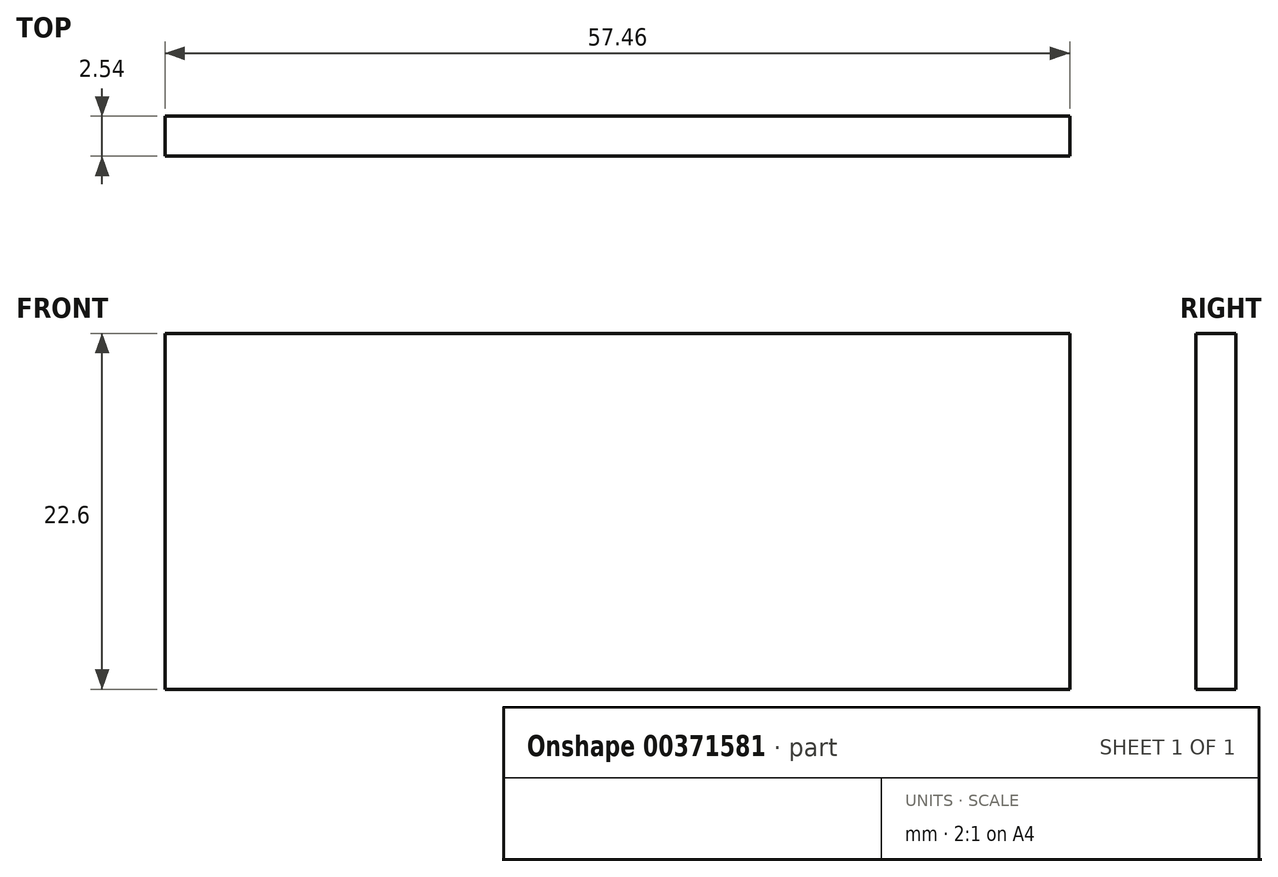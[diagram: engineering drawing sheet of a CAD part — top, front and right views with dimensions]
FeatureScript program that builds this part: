
annotation { "Feature Type Name" : "Feature", "Feature Type Description" : "" }
export const myFeature = defineFeature(function(context is Context, id is Id, definition is map)
    precondition{}
    {
        {
            var Q0;
            Q0=qCreatedBy(makeId("Front.planeOp"),FACE);
            var sketch = newSketch(context, id + "F0", { "sketchPlane" : qUnion([Q0])});
            skLineSegment(sketch, "E0.bottom", {"start": v(28.73, -11.3) * mm, "end": v(-28.73, -11.3) * mm});
            skLineSegment(sketch, "E0.top", {"start": v(28.73, 11.3) * mm, "end": v(-28.73, 11.3) * mm});
            skLineSegment(sketch, "E0.left", {"start": v(28.73, -11.3) * mm, "end": v(28.73, 11.3) * mm});
            skLineSegment(sketch, "E0.right", {"start": v(-28.73, -11.3) * mm, "end": v(-28.73, 11.3) * mm});
            skPoint(sketch, "E0.middle", {"position": v(0, 0) * mm});
            skSolve(sketch);
        }
        {
            var Q0;
            Q0=makeQuery(id+"F0.imprint","IMPRINT",FACE,{"disambiguationData":[TD([[makeQuery(id+"F0.imprint","IMPRINT",EDGE,{"derivedFrom":sQuery(id+"F0.wireOp",EDGE,"E0.bottom")}),-1.0]])]});
            extrude(context, id + "F1", {"entities" : qUnion([Q0]), "depth" : 2.54 * mm});
        }
    });
